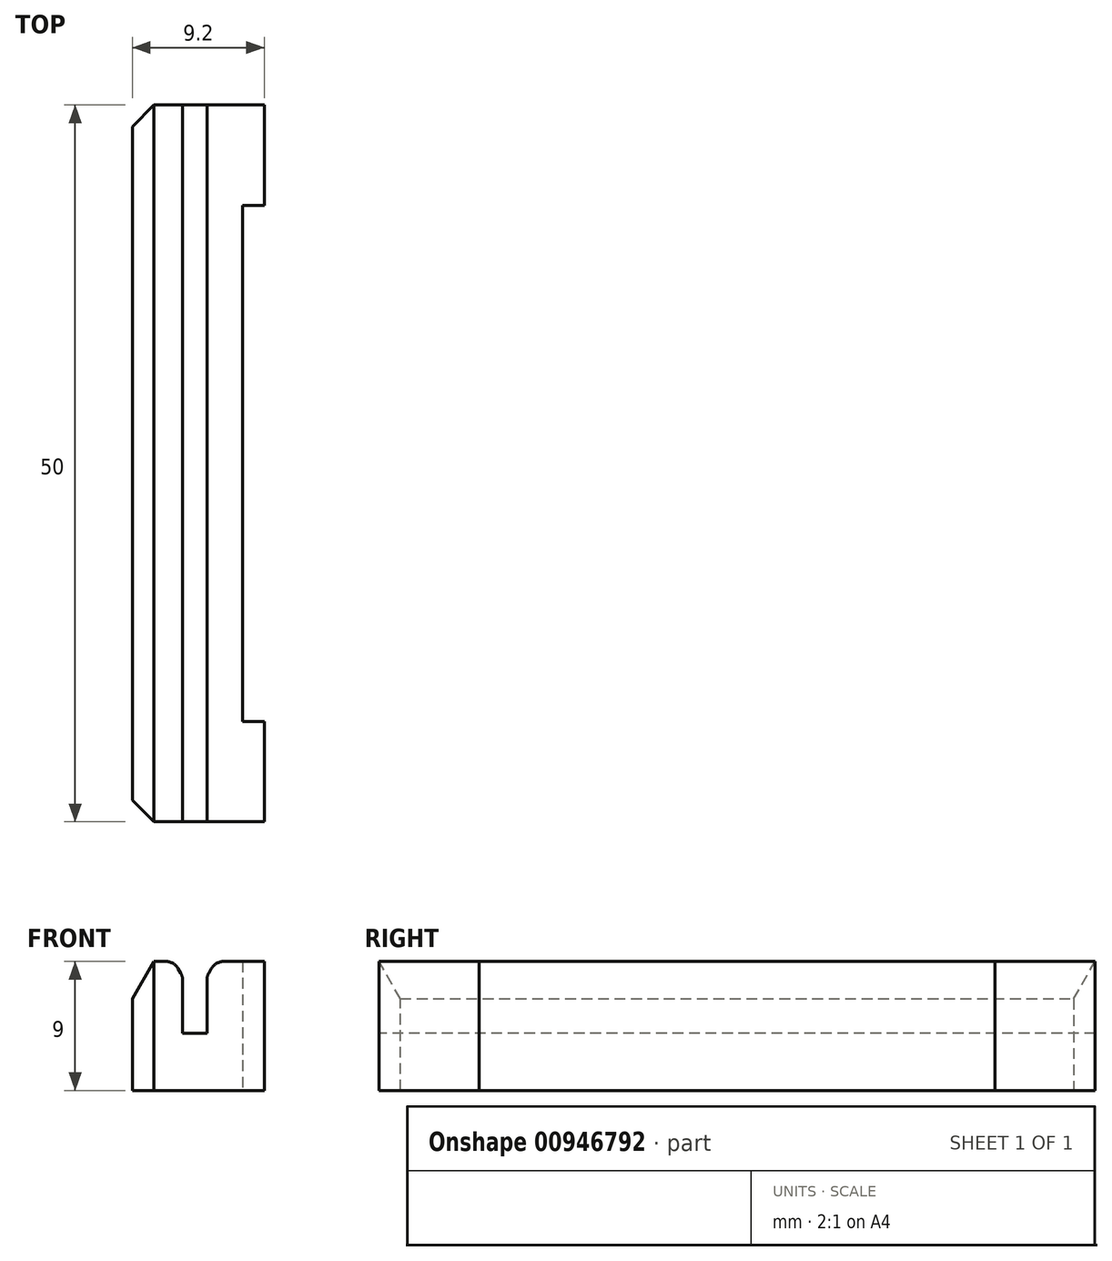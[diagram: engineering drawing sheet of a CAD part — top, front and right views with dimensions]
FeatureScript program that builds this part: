
annotation { "Feature Type Name" : "Feature", "Feature Type Description" : "" }
export const myFeature = defineFeature(function(context is Context, id is Id, definition is map)
    precondition{}
    {
        {
            var Q0;
            Q0=qCreatedBy(makeId("Front.planeOp"),FACE);
            var sketch = newSketch(context, id + "F0", { "sketchPlane" : qUnion([Q0])});
            skLineSegment(sketch, "E0.bottom", {"start": v(0.85, -2.5) * mm, "end": v(-0.85, -2.5) * mm});
            skLineSegment(sketch, "E0.left", {"start": v(0.85, -2.5) * mm, "end": v(0.85, 2.5) * mm});
            skLineSegment(sketch, "E0.right", {"start": v(-0.85, -2.5) * mm, "end": v(-0.85, 2.5) * mm});
            skPoint(sketch, "E0.middle", {"position": v(0, 0) * mm});
            skLineSegment(sketch, "E1", {"start": v(-0.85, 2.5) * mm, "end": v(-3.35, 2.5) * mm});
            skLineSegment(sketch, "E2", {"start": v(-3.35, 2.5) * mm, "end": v(-3.35, -6.5) * mm});
            skLineSegment(sketch, "E3", {"start": v(-3.35, -6.5) * mm, "end": v(3.35, -6.5) * mm});
            skLineSegment(sketch, "E4", {"start": v(3.35, -6.5) * mm, "end": v(3.35, 2.5) * mm});
            skLineSegment(sketch, "E5", {"start": v(3.35, 2.5) * mm, "end": v(0.85, 2.5) * mm});
            skLineSegment(sketch, "E6", {"start": v(0, 0) * mm, "end": v(0, 11.27) * mm, "construction": true});
            skSolve(sketch);
        }
        {
            var Q0;
            Q0 = qSketchRegion(id + "F0", true);
            extrude(context, id + "F1", {"entities" : qUnion([Q0]), "endBound" : BoundingType.SYMMETRIC, "oppositeDirection" : true, "depth" : 50 * mm, "offsetDistance" : 25 * mm});
        }
        {
            var Q0;
            Q0=makeQuery(id+"F1.opExtrude","SWEPT_EDGE",EDGE,{"disambiguationData":[OSD([sQuery(id+"F0.wireOp",EDGE,"E0.right"),sQuery(id+"F0.wireOp",EDGE,"E1")])]});
            chamfer(context, id + "F2", {"entities" : qUnion([Q0]), "chamferType" : ChamferType.OFFSET_ANGLE, "width" : .6 * mm, "oppositeDirection" : true, "angle" : 60 * degree, "tangentPropagation" : true});
        }
        {
            var Q0;
            Q0=makeQuery(id+"F1.opExtrude","SWEPT_EDGE",EDGE,{"disambiguationData":[OSD([sQuery(id+"F0.wireOp",EDGE,"E0.left"),sQuery(id+"F0.wireOp",EDGE,"E5")])]});
            chamfer(context, id + "F3", {"entities" : qUnion([Q0]), "chamferType" : ChamferType.OFFSET_ANGLE, "width" : .6 * mm, "oppositeDirection" : false, "angle" : 60 * degree, "tangentPropagation" : true});
        }
        {
            var Q0;
            Q0=makeQuery(id+"F1.opExtrude","SWEPT_FACE",FACE,{"disambiguationData":[OSD([sQuery(id+"F0.wireOp",EDGE,"E4")])]});
            var sketch = newSketch(context, id + "F4", { "sketchPlane" : qUnion([Q0])});
            skLineSegment(sketch, "E7.bottom", {"start": v(-25, 2.5) * mm, "end": v(-18, 2.5) * mm});
            skLineSegment(sketch, "E7.top", {"start": v(-25, -6.5) * mm, "end": v(-18, -6.5) * mm});
            skLineSegment(sketch, "E7.left", {"start": v(-25, 2.5) * mm, "end": v(-25, -6.5) * mm});
            skLineSegment(sketch, "E7.right", {"start": v(-18, 2.5) * mm, "end": v(-18, -6.5) * mm});
            skLineSegment(sketch, "E8", {"start": v(0, 0) * mm, "end": v(0, -11.36) * mm, "construction": true});
            skLineSegment(sketch, "E9.MirrorCS", {"start": v(25, 2.5) * mm, "end": v(25, -6.5) * mm});
            skLineSegment(sketch, "E10.MirrorCS", {"start": v(25, 2.5) * mm, "end": v(18, 2.5) * mm});
            skLineSegment(sketch, "E11.MirrorCS", {"start": v(25, -6.5) * mm, "end": v(18, -6.5) * mm});
            skLineSegment(sketch, "E12.MirrorCS", {"start": v(18, 2.5) * mm, "end": v(18, -6.5) * mm});
            skSolve(sketch);
        }
        {
            var Q0;
            Q0 = qSketchRegion(id + "F4", true);
            extrude(context, id + "F5", {"entities" : qUnion([Q0]), "operationType" : NewBodyOperationType.ADD, "depth" : 1.5 * mm, "offsetDistance" : 25 * mm});
        }
        {
            var Q0;
            Q0=makeQuery(id+"F1.opExtrude","SWEPT_FACE",FACE,{"disambiguationData":[OSD([sQuery(id+"F0.wireOp",EDGE,"E2")])]});
            var sketch = newSketch(context, id + "F6", { "sketchPlane" : qUnion([Q0])});
            skLineSegment(sketch, "E13.0", {"start": v(-25, 2.5) * mm, "end": v(25, 2.5) * mm});
            skLineSegment(sketch, "E13.1", {"start": v(25, 2.5) * mm, "end": v(25, -6.5) * mm});
            skLineSegment(sketch, "E13.2", {"start": v(-25, -6.5) * mm, "end": v(25, -6.5) * mm});
            skLineSegment(sketch, "E13.3", {"start": v(-25, 2.5) * mm, "end": v(-25, -6.5) * mm});
            skSolve(sketch);
        }
        {
            var Q0;
            Q0 = qSketchRegion(id + "F6", true);
            extrude(context, id + "F7", {"entities" : qUnion([Q0]), "operationType" : NewBodyOperationType.ADD, "depth" : 1 * mm, "offsetDistance" : 25 * mm});
        }
        {
            var Q0;
            Q0=makeQuery(id+"F7.opExtrude","CAP_EDGE",EDGE,{"disambiguationData":[OSD([sQuery(id+"F6.wireOp",EDGE,"E13.0")])],"isStart":false});
            chamfer(context, id + "F8", {"entities" : qUnion([Q0]), "chamferType" : ChamferType.OFFSET_ANGLE, "width" : 1.5 * mm, "oppositeDirection" : false, "angle" : 60 * degree, "tangentPropagation" : true});
        }
        {
            var Q0;
            Q0=makeQuery(id+"F7.opExtrude","CAP_EDGE",EDGE,{"disambiguationData":[OSD([sQuery(id+"F6.wireOp",EDGE,"E13.1")])],"isStart":false});
            var Q1;
            Q1=makeQuery(id+"F7.opExtrude","CAP_EDGE",EDGE,{"disambiguationData":[OSD([sQuery(id+"F6.wireOp",EDGE,"E13.3")])],"isStart":false});
            chamfer(context, id + "F9", {"entities" : qUnion([Q0, Q1]), "width" : 1.5 * mm, "tangentPropagation" : true});
        }
        {
            var Q0;
            {var subQ0=sQuery(id+"F0.wireOp",EDGE,"E0.right");Q0=makeQuery(id+"F2.opChamfer","BLEND_EDGE",EDGE,{"blendedFrom":[makeQuery(id+"F1.opExtrude","SWEPT_EDGE",EDGE,{"disambiguationData":[OSD([subQ0,sQuery(id+"F0.wireOp",EDGE,"E1")])]}),makeQuery(id+"F1.opExtrude","SWEPT_FACE",FACE,{"disambiguationData":[OSD([subQ0])]})],"blendedInto":[makeQuery(id+"F1.opExtrude","SWEPT_FACE",FACE,{"disambiguationData":[OSD([subQ0])]})]});}
            var Q1;
            {var subQ0=sQuery(id+"F0.wireOp",EDGE,"E1");Q1=makeQuery(id+"F2.opChamfer","BLEND_EDGE",EDGE,{"blendedFrom":[makeQuery(id+"F1.opExtrude","SWEPT_EDGE",EDGE,{"disambiguationData":[OSD([sQuery(id+"F0.wireOp",EDGE,"E0.right"),subQ0])]}),makeQuery(id+"F1.opExtrude","SWEPT_FACE",FACE,{"disambiguationData":[OSD([subQ0])]})],"blendedInto":[makeQuery(id+"F1.opExtrude","SWEPT_FACE",FACE,{"disambiguationData":[OSD([subQ0])]})]});}
            var Q2;
            {var subQ0=sQuery(id+"F0.wireOp",EDGE,"E5");Q2=makeQuery(id+"F3.opChamfer","BLEND_EDGE",EDGE,{"blendedFrom":[makeQuery(id+"F1.opExtrude","SWEPT_EDGE",EDGE,{"disambiguationData":[OSD([sQuery(id+"F0.wireOp",EDGE,"E0.left"),subQ0])]}),makeQuery(id+"F1.opExtrude","SWEPT_FACE",FACE,{"disambiguationData":[OSD([subQ0])]})],"blendedInto":[makeQuery(id+"F1.opExtrude","SWEPT_FACE",FACE,{"disambiguationData":[OSD([subQ0])]})]});}
            var Q3;
            {var subQ0=sQuery(id+"F0.wireOp",EDGE,"E0.left");Q3=makeQuery(id+"F3.opChamfer","BLEND_EDGE",EDGE,{"blendedFrom":[makeQuery(id+"F1.opExtrude","SWEPT_EDGE",EDGE,{"disambiguationData":[OSD([subQ0,sQuery(id+"F0.wireOp",EDGE,"E5")])]}),makeQuery(id+"F1.opExtrude","SWEPT_FACE",FACE,{"disambiguationData":[OSD([subQ0])]})],"blendedInto":[makeQuery(id+"F1.opExtrude","SWEPT_FACE",FACE,{"disambiguationData":[OSD([subQ0])]})]});}
            fillet(context, id + "F10", {"entities" : qUnion([Q0, Q1, Q2, Q3]), "radius" : 1 * mm, "tangentPropagation" : true, "allowEdgeOverflow" : false});
        }
    });
